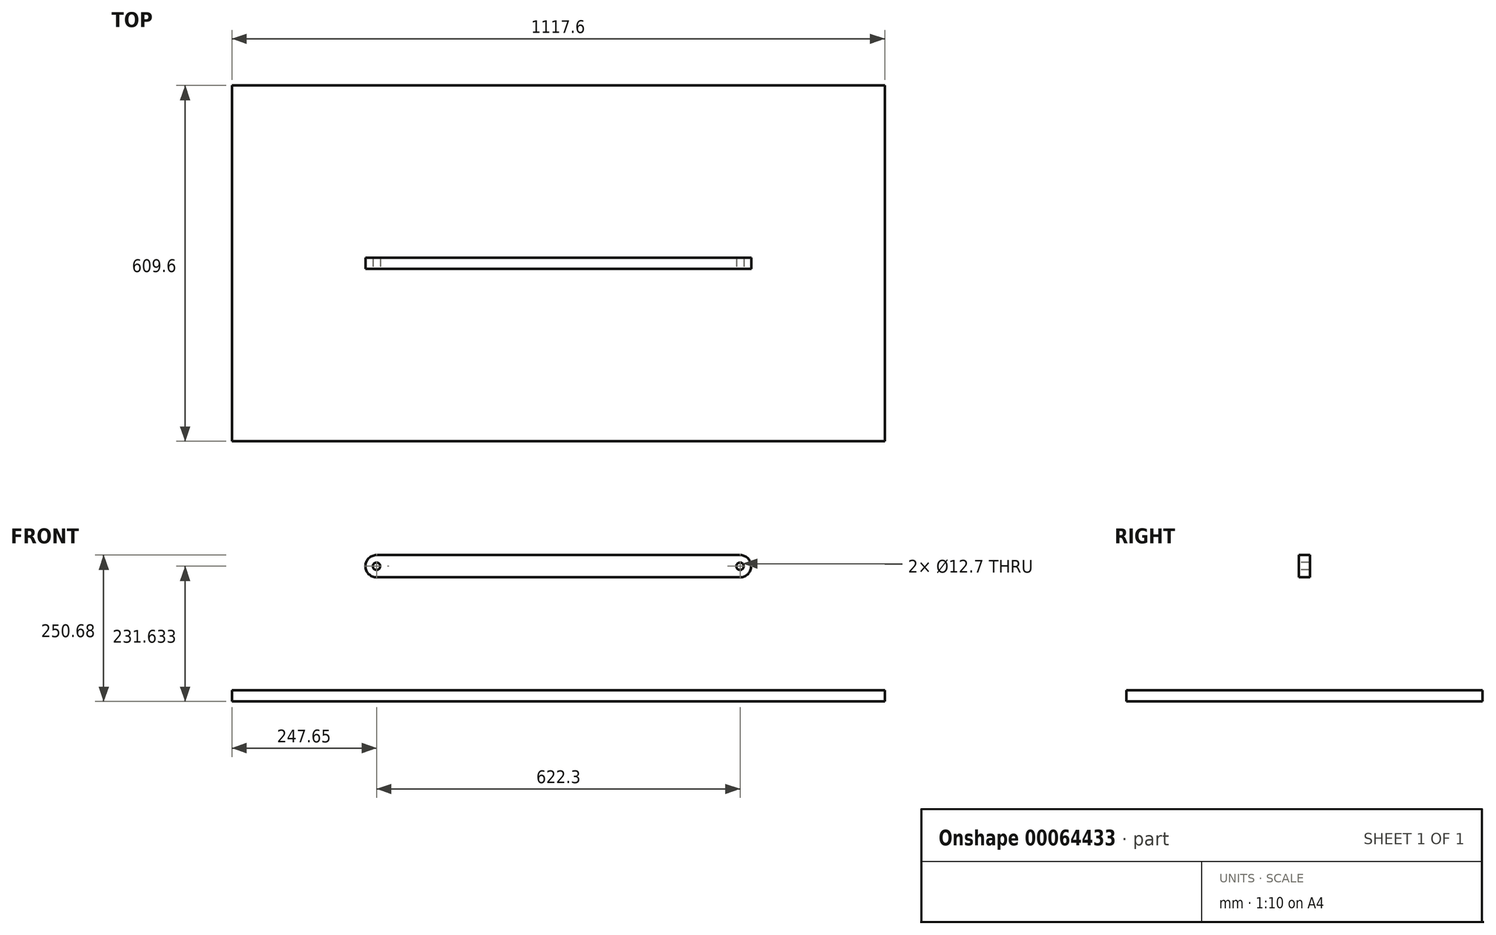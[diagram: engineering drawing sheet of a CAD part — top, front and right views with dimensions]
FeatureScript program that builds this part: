
annotation { "Feature Type Name" : "Feature", "Feature Type Description" : "" }
export const myFeature = defineFeature(function(context is Context, id is Id, definition is map)
    precondition{}
    {
        {
            var Q0;
            Q0=qCreatedBy(makeId("Top.planeOp"),FACE);
            var sketch = newSketch(context, id + "F0", { "sketchPlane" : qUnion([Q0])});
            skLineSegment(sketch, "E0.rect.bottom", {"start": v(558.8, -304.8) * mm, "end": v(-558.8, -304.8) * mm});
            skLineSegment(sketch, "E0.rect.top", {"start": v(558.8, 304.8) * mm, "end": v(-558.8, 304.8) * mm});
            skLineSegment(sketch, "E0.rect.left", {"start": v(558.8, -304.8) * mm, "end": v(558.8, 304.8) * mm});
            skLineSegment(sketch, "E0.rect.right", {"start": v(-558.8, -304.8) * mm, "end": v(-558.8, 304.8) * mm});
            skPoint(sketch, "E0.rect.middle", {"position": v(0, 0) * mm});
            skSolve(sketch);
        }
        {
            var Q0;
            Q0=makeQuery(id+"F0.imprint","IMPRINT",FACE,{"disambiguationData":[TD([[makeQuery(id+"F0.imprint","IMPRINT",EDGE,{"derivedFrom":sQuery(id+"F0.wireOp",EDGE,"E0.rect.bottom")}),-1.0]])]});
            extrude(context, id + "F1", {"entities" : qUnion([Q0]), "depth" : 19.05 * mm});
        }
        {
            var Q0;
            Q0=qCreatedBy(makeId("Front.planeOp"),FACE);
            var sketch = newSketch(context, id + "F2", { "sketchPlane" : qUnion([Q0])});
            skLineSegment(sketch, "E1.rect.bottom", {"start": v(330.2, 212.58) * mm, "end": v(-330.2, 212.58) * mm});
            skLineSegment(sketch, "E1.rect.top", {"start": v(330.2, 250.68) * mm, "end": v(-330.2, 250.68) * mm});
            skLineSegment(sketch, "E1.rect.left", {"start": v(330.2, 212.58) * mm, "end": v(330.2, 250.68) * mm});
            skLineSegment(sketch, "E1.rect.right", {"start": v(-330.2, 212.58) * mm, "end": v(-330.2, 250.68) * mm});
            skPoint(sketch, "E1.rect.middle", {"position": v(0, 231.63) * mm});
            skSolve(sketch);
        }
        {
            var Q0;
            Q0=makeQuery(id+"F2.imprint","IMPRINT",FACE,{"disambiguationData":[TD([[makeQuery(id+"F2.imprint","IMPRINT",EDGE,{"derivedFrom":sQuery(id+"F2.wireOp",EDGE,"E1.rect.bottom")}),-1.0]])]});
            extrude(context, id + "F3", {"entities" : qUnion([Q0]), "endBound" : BoundingType.SYMMETRIC, "depth" : 19.05 * mm});
        }
        {
            var Q0;
            Q0=makeQuery(id+"F3.opExtrude","SWEPT_EDGE",EDGE,{"disambiguationData":[OSD([sQuery(id+"F2.wireOp",EDGE,"E1.rect.top"),sQuery(id+"F2.wireOp",EDGE,"E1.rect.left")])]});
            var Q1;
            Q1=makeQuery(id+"F3.opExtrude","SWEPT_EDGE",EDGE,{"disambiguationData":[OSD([sQuery(id+"F2.wireOp",EDGE,"E1.rect.bottom"),sQuery(id+"F2.wireOp",EDGE,"E1.rect.left")])]});
            var Q2;
            Q2=makeQuery(id+"F3.opExtrude","SWEPT_EDGE",EDGE,{"disambiguationData":[OSD([sQuery(id+"F2.wireOp",EDGE,"E1.rect.top"),sQuery(id+"F2.wireOp",EDGE,"E1.rect.right")])]});
            var Q3;
            Q3=makeQuery(id+"F3.opExtrude","SWEPT_EDGE",EDGE,{"disambiguationData":[OSD([sQuery(id+"F2.wireOp",EDGE,"E1.rect.bottom"),sQuery(id+"F2.wireOp",EDGE,"E1.rect.right")])]});
            fillet(context, id + "F4", {"entities" : qUnion([Q0, Q1, Q2, Q3]), "radius" : 19.05 * mm, "tangentPropagation" : true, "allowEdgeOverflow" : false});
        }
        {
            var Q0;
            Q0=makeQuery(id+"F3.opExtrude","CAP_FACE",FACE,{"disambiguationData":[OSD([sQuery(id+"F2.wireOp",EDGE,"E1.rect.bottom"),sQuery(id+"F2.wireOp",EDGE,"E1.rect.top"),sQuery(id+"F2.wireOp",EDGE,"E1.rect.left"),sQuery(id+"F2.wireOp",EDGE,"E1.rect.right")])],"isStart":false});
            var sketch = newSketch(context, id + "F5", { "sketchPlane" : qUnion([Q0])});
            skCircle(sketch, "E2", {"center": v(-311.15, 231.63) * mm, "radius": 6.35 * mm});
            skCircle(sketch, "E3", {"center": v(311.15, 231.63) * mm, "radius": 6.35 * mm});
            skSolve(sketch);
        }
        {
            var Q0;
            Q0=makeQuery(id+"F5.imprint","IMPRINT",FACE,{"disambiguationData":[TD([[makeQuery(id+"F5.imprint","IMPRINT",EDGE,{"derivedFrom":sQuery(id+"F5.wireOp",EDGE,"E2")}),1.0]])]});
            var Q1;
            Q1=makeQuery(id+"F5.imprint","IMPRINT",FACE,{"disambiguationData":[TD([[makeQuery(id+"F5.imprint","IMPRINT",EDGE,{"derivedFrom":sQuery(id+"F5.wireOp",EDGE,"E3")}),1.0]])]});
            extrude(context, id + "F6", {"entities" : qUnion([Q0, Q1]), "operationType" : NewBodyOperationType.REMOVE, "endBound" : BoundingType.THROUGH_ALL, "oppositeDirection" : true, "depth" : 25.4 * mm});
        }
    });
